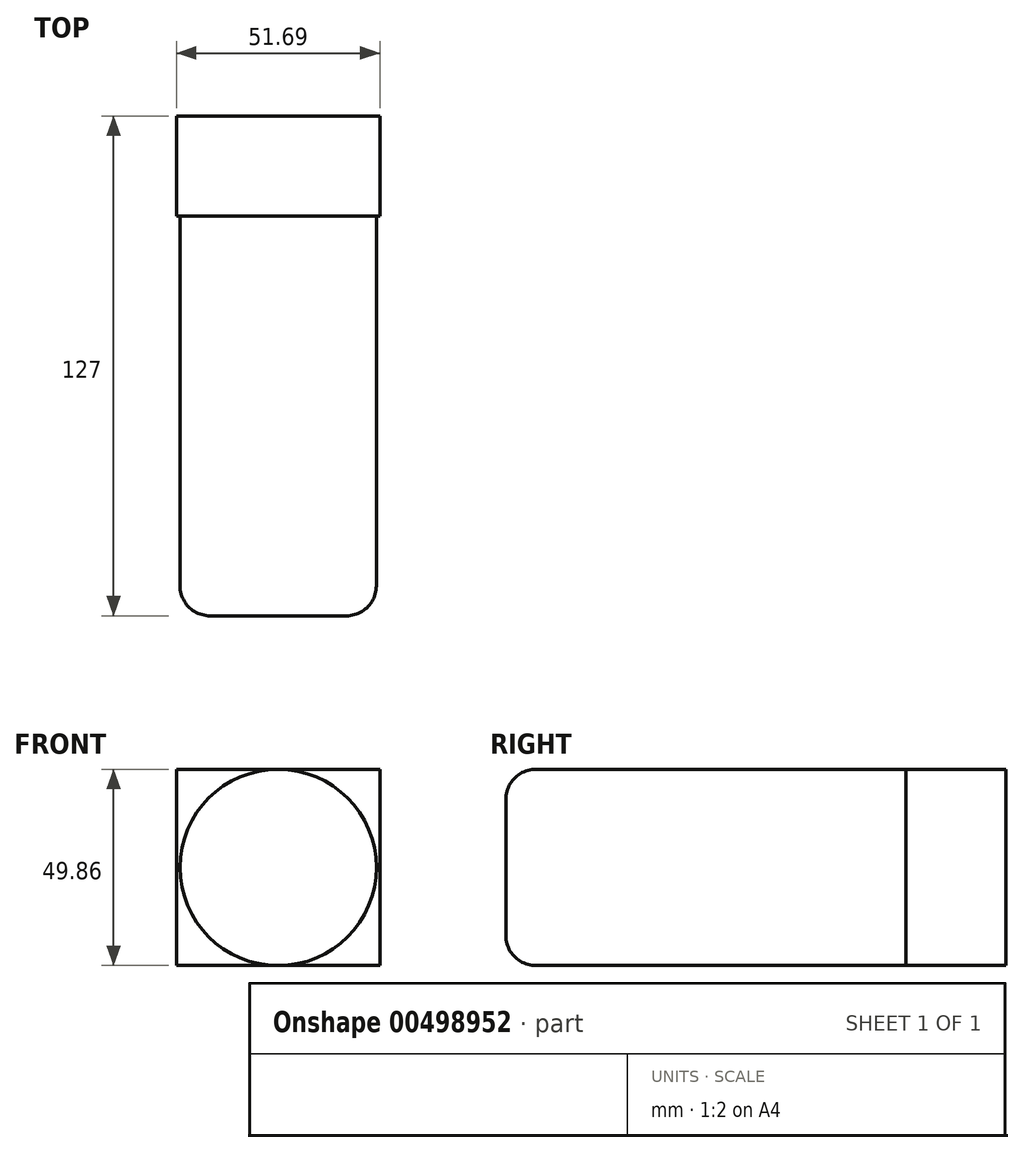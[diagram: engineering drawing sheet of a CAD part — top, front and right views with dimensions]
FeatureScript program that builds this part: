
annotation { "Feature Type Name" : "Feature", "Feature Type Description" : "" }
export const myFeature = defineFeature(function(context is Context, id is Id, definition is map)
    precondition{}
    {
        {
            var Q0;
            Q0=qCreatedBy(makeId("Front.planeOp"),FACE);
            var sketch = newSketch(context, id + "F0", { "sketchPlane" : qUnion([Q0])});
            skLineSegment(sketch, "E0.bottom", {"start": v(-31.16, 122.08) * mm, "end": v(20.53, 122.08) * mm});
            skLineSegment(sketch, "E0.top", {"start": v(-31.16, 171.94) * mm, "end": v(20.53, 171.94) * mm});
            skLineSegment(sketch, "E0.left", {"start": v(-31.16, 122.08) * mm, "end": v(-31.16, 171.94) * mm});
            skLineSegment(sketch, "E0.right", {"start": v(20.53, 122.08) * mm, "end": v(20.53, 171.94) * mm});
            skSolve(sketch);
        }
        {
            var Q0;
            Q0 = qSketchRegion(id + "F0", true);
            extrude(context, id + "F1", {"entities" : qUnion([Q0]), "depth" : 25.4 * mm});
        }
        {
            var Q0;
            Q0=makeQuery(id+"F1.opExtrude","CAP_FACE",FACE,{"disambiguationData":[OSD([sQuery(id+"F0.wireOp",EDGE,"E0.bottom"),sQuery(id+"F0.wireOp",EDGE,"E0.top"),sQuery(id+"F0.wireOp",EDGE,"E0.left"),sQuery(id+"F0.wireOp",EDGE,"E0.right")])],"isStart":false});
            var sketch = newSketch(context, id + "F2", { "sketchPlane" : qUnion([Q0])});
            skCircle(sketch, "E1", {"center": v(-5.32, 147.01) * mm, "radius": 24.93 * mm});
            skPoint(sketch, "E1.centerSnap0", {"position": v(-5.32, 122.08) * mm});
            skPoint(sketch, "E1.centerSnap1", {"position": v(20.53, 147.01) * mm});
            skSolve(sketch);
        }
        {
            var Q0;
            Q0 = qSketchRegion(id + "F2", true);
            extrude(context, id + "F3", {"entities" : qUnion([Q0]), "operationType" : NewBodyOperationType.ADD, "depth" : 76.2 * mm});
        }
        {
            var Q0;
            Q0=makeQuery(id+"F3.opExtrude","CAP_FACE",FACE,{"disambiguationData":[OSD([sQuery(id+"F2.wireOp",EDGE,"E1")])],"isStart":false});
            var sketch = newSketch(context, id + "F4", { "sketchPlane" : qUnion([Q0])});
            skSolve(sketch);
        }
        {
            var Q0;
            Q0 = qSketchRegion(id + "F4", true);
            var Q1;
            Q1=makeQuery(id+"F4.imprint","IMPRINT",FACE,{"disambiguationData":[TD([[makeQuery(id+"F4.imprint","IMPRINT",EDGE,{"derivedFrom":makeQuery(id+"F3.opExtrude","CAP_EDGE",EDGE,{"disambiguationData":[OSD([sQuery(id+"F2.wireOp",EDGE,"E1")])],"isStart":false})}),1.0]])]});
            extrude(context, id + "F5", {"entities" : qUnion([Q0, Q1]), "operationType" : NewBodyOperationType.ADD, "depth" : 25.4 * mm});
        }
        {
            var Q0;
            Q0=makeQuery(id+"F5.opExtrude","CAP_EDGE",EDGE,{"disambiguationData":[OSD([sQuery(id+"F2.wireOp",EDGE,"E1")])],"isStart":false});
            fillet(context, id + "F6", {"entities" : qUnion([Q0]), "radius" : 7.62 * mm, "tangentPropagation" : true, "allowEdgeOverflow" : false});
        }
    });
